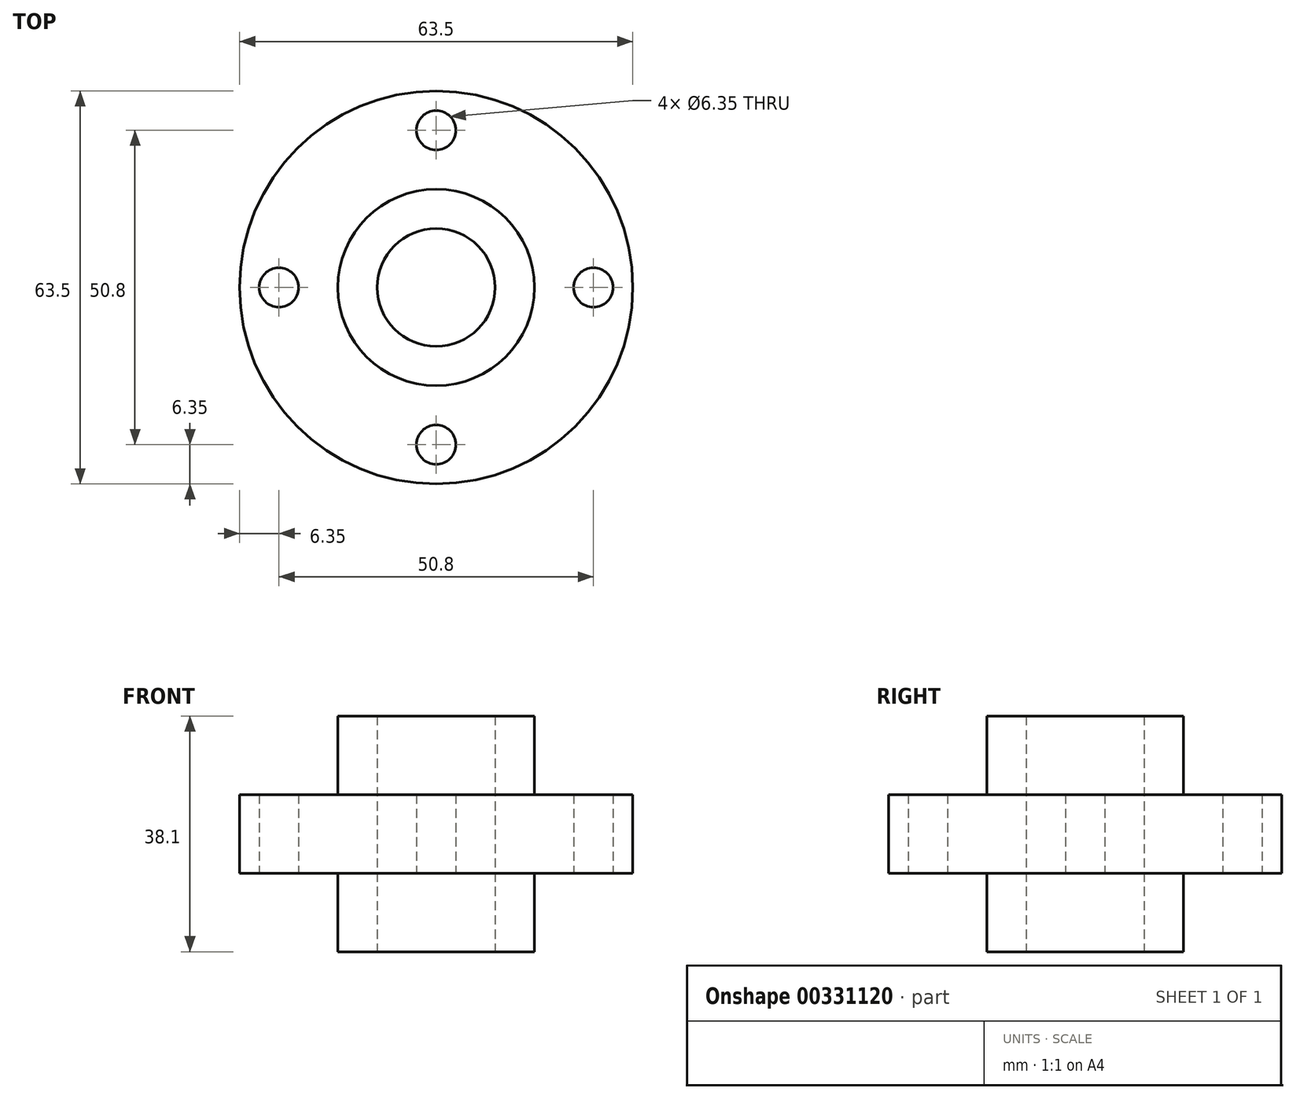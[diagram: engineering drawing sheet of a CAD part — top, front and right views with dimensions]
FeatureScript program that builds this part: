
annotation { "Feature Type Name" : "Feature", "Feature Type Description" : "" }
export const myFeature = defineFeature(function(context is Context, id is Id, definition is map)
    precondition{}
    {
        {
            var Q0;
            Q0=qCreatedBy(makeId("Top.planeOp"),FACE);
            var sketch = newSketch(context, id + "F0", { "sketchPlane" : qUnion([Q0])});
            skCircle(sketch, "E0", {"center": v(0, 0) * mm, "radius": 9.53 * mm});
            skCircle(sketch, "E1", {"center": v(0, 0) * mm, "radius": 25.4 * mm, "construction": true});
            skCircle(sketch, "E2", {"center": v(0, 0) * mm, "radius": 31.75 * mm});
            skCircle(sketch, "E3", {"center": v(0, 25.4) * mm, "radius": 3.18 * mm});
            skCircle(sketch, "E4", {"center": v(25.4, 0) * mm, "radius": 3.18 * mm});
            skCircle(sketch, "E5", {"center": v(0, -25.4) * mm, "radius": 3.18 * mm});
            skCircle(sketch, "E6", {"center": v(-25.4, 0) * mm, "radius": 3.17 * mm});
            skSolve(sketch);
        }
        {
            var Q0;
            Q0 = qSketchRegion(id + "F0", true);
            extrude(context, id + "F1", {"entities" : qUnion([Q0]), "depth" : 12.7 * mm});
        }
        {
            var Q0;
            Q0=makeQuery(id+"F1.opExtrude","CAP_FACE",FACE,{"disambiguationData":[OSD([sQuery(id+"F0.wireOp",EDGE,"E0"),sQuery(id+"F0.wireOp",EDGE,"E2"),sQuery(id+"F0.wireOp",EDGE,"E3"),sQuery(id+"F0.wireOp",EDGE,"E4"),sQuery(id+"F0.wireOp",EDGE,"E5"),sQuery(id+"F0.wireOp",EDGE,"E6")])],"isStart":false});
            var sketch = newSketch(context, id + "F2", { "sketchPlane" : qUnion([Q0])});
            skCircle(sketch, "E7", {"center": v(0, 0) * mm, "radius": 15.88 * mm});
            skCircle(sketch, "E8", {"center": v(0, 0) * mm, "radius": 9.53 * mm});
            skSolve(sketch);
        }
        {
            var Q0;
            Q0 = qSketchRegion(id + "F2", true);
            extrude(context, id + "F3", {"entities" : qUnion([Q0]), "operationType" : NewBodyOperationType.ADD, "depth" : 12.7 * mm, "hasSecondDirection" : true, "secondDirectionOppositeDirection" : true, "secondDirectionDepth" : 25.4 * mm});
        }
    });
